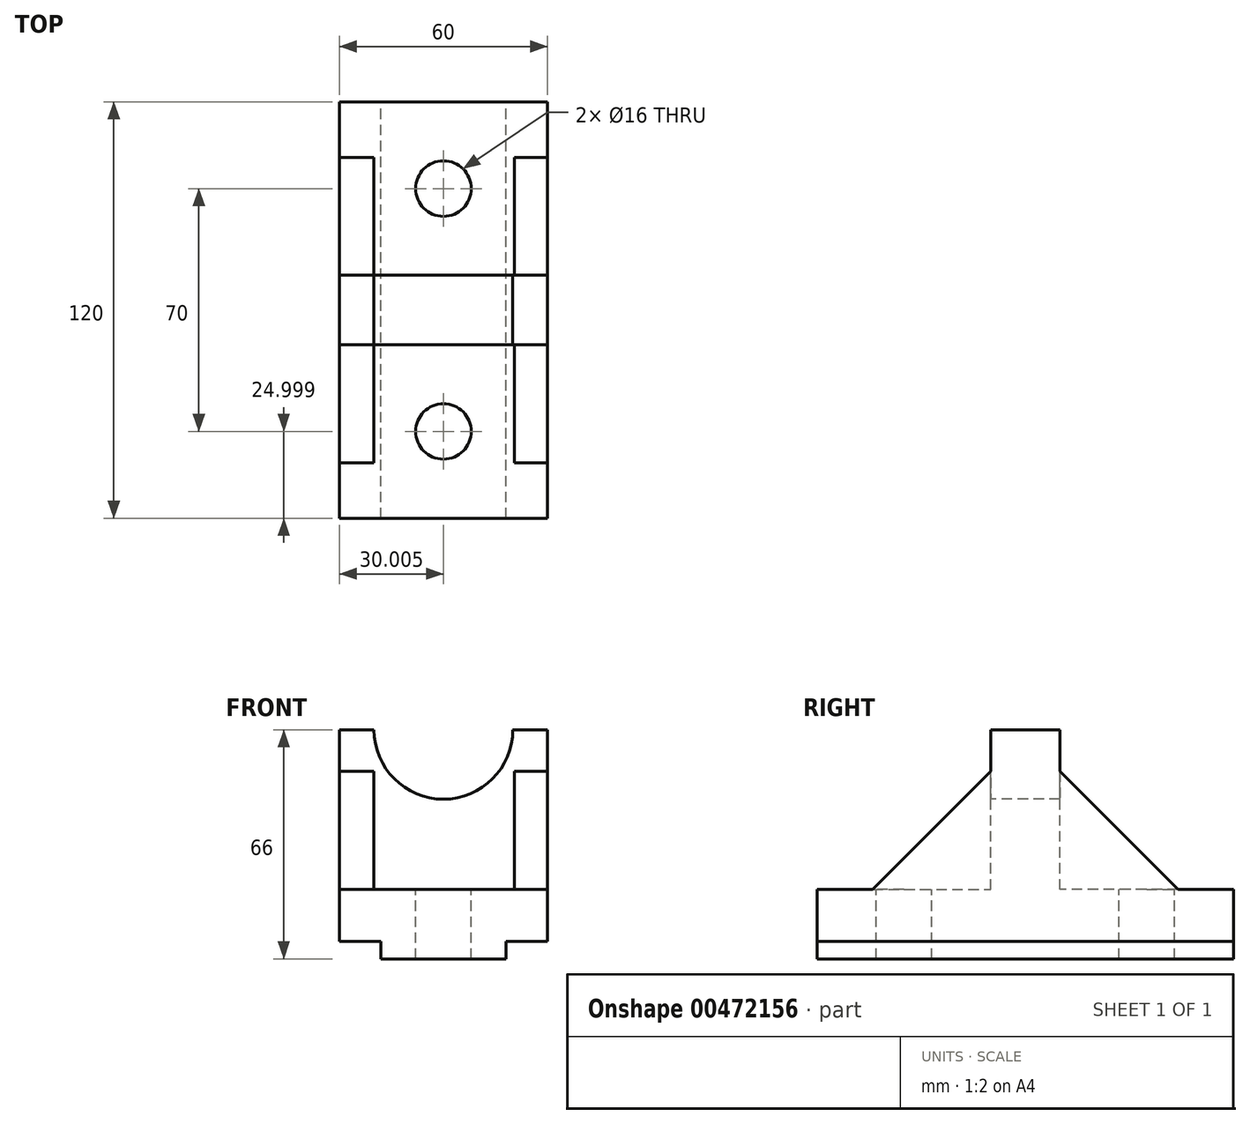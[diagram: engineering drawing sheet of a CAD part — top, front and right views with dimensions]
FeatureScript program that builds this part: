
annotation { "Feature Type Name" : "Feature", "Feature Type Description" : "" }
export const myFeature = defineFeature(function(context is Context, id is Id, definition is map)
    precondition{}
    {
        {
            var Q0;
            Q0=qCreatedBy(makeId("Top.planeOp"),FACE);
            var sketch = newSketch(context, id + "F0", { "sketchPlane" : qUnion([Q0])});
            skLineSegment(sketch, "E0.bottom", {"start": v(-50.39, 77.64) * mm, "end": v(9.61, 77.64) * mm});
            skLineSegment(sketch, "E0.top", {"start": v(-50.39, -42.36) * mm, "end": v(9.61, -42.36) * mm});
            skLineSegment(sketch, "E0.left", {"start": v(-50.39, 77.64) * mm, "end": v(-50.39, -42.36) * mm});
            skLineSegment(sketch, "E0.right", {"start": v(9.61, 77.64) * mm, "end": v(9.61, -42.36) * mm});
            skSolve(sketch);
        }
        {
            var Q0;
            Q0 = qSketchRegion(id + "F0", true);
            extrude(context, id + "F1", {"entities" : qUnion([Q0]), "depth" : 20 * mm});
        }
        {
            var Q0;
            Q0=makeQuery(id+"F1.opExtrude","SWEPT_FACE",FACE,{"disambiguationData":[OSD([sQuery(id+"F0.wireOp",EDGE,"E0.top")])]});
            var sketch = newSketch(context, id + "F2", { "sketchPlane" : qUnion([Q0])});
            skLineSegment(sketch, "E1", {"start": v(-50.39, 0) * mm, "end": v(-38.39, 0) * mm});
            skLineSegment(sketch, "E2", {"start": v(-38.39, 0) * mm, "end": v(-2.39, 0) * mm});
            skLineSegment(sketch, "E3", {"start": v(-2.39, 0) * mm, "end": v(9.61, 0) * mm});
            skSolve(sketch);
        }
        {
            var Q0;
            Q0=makeQuery(id+"F0.imprint","IMPRINT",FACE,{"disambiguationData":[TD([[makeQuery(id+"F0.imprint","IMPRINT",EDGE,{"derivedFrom":sQuery(id+"F0.wireOp",EDGE,"E0.bottom")}),-1.0]])]});
            var sketch = newSketch(context, id + "F3", { "sketchPlane" : qUnion([Q0])});
            skPoint(sketch, "E4.0", {"position": v(-2.39, -42.36) * mm});
            skPoint(sketch, "E5.0", {"position": v(-38.39, -42.36) * mm});
            skLineSegment(sketch, "E6.0", {"start": v(-50.39, 77.64) * mm, "end": v(9.61, 77.64) * mm});
            skLineSegment(sketch, "E7", {"start": v(-38.39, -42.36) * mm, "end": v(-38.39, 77.64) * mm});
            skLineSegment(sketch, "E8", {"start": v(-2.39, -42.36) * mm, "end": v(-2.39, 77.64) * mm});
            skSolve(sketch);
        }
        {
            var Q0;
            {var subQ2=sQuery(id+"F3.wireOp",EDGE,"E7");Q0=makeQuery(id+"F3.imprint","IMPRINT",FACE,{"disambiguationData":[TD([[makeQuery(id+"F3.imprint","IMPRINT",EDGE,{"derivedFrom":subQ2}),1.0]])]});}
            var Q1;
            {var subQ2=sQuery(id+"F3.wireOp",EDGE,"E8");Q1=makeQuery(id+"F3.imprint","IMPRINT",FACE,{"disambiguationData":[TD([[makeQuery(id+"F3.imprint","IMPRINT",EDGE,{"derivedFrom":subQ2}),-1.0]])]});}
            extrude(context, id + "F4", {"entities" : qUnion([Q0, Q1]), "operationType" : NewBodyOperationType.REMOVE, "depth" : 5 * mm});
        }
        {
            var Q0;
            Q0=makeQuery(id+"F1.opExtrude","CAP_FACE",FACE,{"disambiguationData":[OSD([sQuery(id+"F0.wireOp",EDGE,"E0.bottom"),sQuery(id+"F0.wireOp",EDGE,"E0.top"),sQuery(id+"F0.wireOp",EDGE,"E0.left"),sQuery(id+"F0.wireOp",EDGE,"E0.right")])],"isStart":false});
            var sketch = newSketch(context, id + "F5", { "sketchPlane" : qUnion([Q0])});
            skLineSegment(sketch, "E9", {"start": v(-20.39, -42.36) * mm, "end": v(-20.39, -17.36) * mm});
            skLineSegment(sketch, "E10", {"start": v(-20.39, -17.36) * mm, "end": v(9.61, -17.36) * mm});
            skCircle(sketch, "E11", {"center": v(-20.39, -17.36) * mm, "radius": 8 * mm});
            skLineSegment(sketch, "E12", {"start": v(-50.39, 17.64) * mm, "end": v(9.61, 17.64) * mm});
            skLineSegment(sketch, "E13.MirrorCS", {"start": v(-20.39, 7.64) * mm, "end": v(-20.39, -17.36) * mm});
            skCircle(sketch, "E14.MirrorC", {"center": v(-20.39, 52.64) * mm, "radius": 8 * mm});
            skSolve(sketch);
        }
        {
            var Q0;
            Q0 = qSketchRegion(id + "F5", true);
            extrude(context, id + "F6", {"entities" : qUnion([Q0]), "operationType" : NewBodyOperationType.REMOVE, "oppositeDirection" : true, "depth" : 45.4 * mm});
        }
        {
            var Q0;
            Q0=makeQuery(id+"F1.opExtrude","CAP_FACE",FACE,{"disambiguationData":[OSD([sQuery(id+"F0.wireOp",EDGE,"E0.bottom"),sQuery(id+"F0.wireOp",EDGE,"E0.top"),sQuery(id+"F0.wireOp",EDGE,"E0.left"),sQuery(id+"F0.wireOp",EDGE,"E0.right")])],"isStart":false});
            var sketch = newSketch(context, id + "F7", { "sketchPlane" : qUnion([Q0])});
            skLineSegment(sketch, "E15", {"start": v(-50.39, -42.36) * mm, "end": v(-50.39, 7.64) * mm});
            skLineSegment(sketch, "E16", {"start": v(-50.39, 7.64) * mm, "end": v(-50.39, 27.64) * mm});
            skLineSegment(sketch, "E17", {"start": v(-50.39, 27.64) * mm, "end": v(-50.39, 77.64) * mm});
            skLineSegment(sketch, "E18", {"start": v(-50.39, 27.64) * mm, "end": v(9.61, 27.64) * mm});
            skLineSegment(sketch, "E19", {"start": v(9.61, 27.64) * mm, "end": v(9.61, 7.64) * mm});
            skLineSegment(sketch, "E20", {"start": v(9.61, 7.64) * mm, "end": v(-50.39, 7.64) * mm});
            skSolve(sketch);
        }
        {
            var Q0;
            Q0 = qSketchRegion(id + "F7", true);
            extrude(context, id + "F8", {"entities" : qUnion([Q0]), "operationType" : NewBodyOperationType.ADD, "depth" : 46 * mm});
        }
        {
            var Q0;
            Q0=makeQuery(id+"F8.opExtrude","SWEPT_FACE",FACE,{"disambiguationData":[OSD([sQuery(id+"F7.wireOp",EDGE,"E20")])]});
            var sketch = newSketch(context, id + "F9", { "sketchPlane" : qUnion([Q0])});
            skLineSegment(sketch, "E21", {"start": v(-20.39, 66) * mm, "end": v(-20.39, 92.8) * mm});
            skLineSegment(sketch, "E22", {"start": v(-20.39, 92.8) * mm, "end": v(-20.39, 22.88) * mm});
            skSolve(sketch);
        }
        {
            var Q0;
            Q0=makeQuery(id+"F8.boolean.opBoolean","MERGE",FACE,{"derivedFrom":[makeQuery(id+"F1.opExtrude","SWEPT_FACE",FACE,{"disambiguationData":[OSD([sQuery(id+"F0.wireOp",EDGE,"E0.left")])]}),makeQuery(id+"F8.opExtrude","SWEPT_FACE",FACE,{"disambiguationData":[OSD([sQuery(id+"F7.wireOp",EDGE,"E16")])]})]});
            var sketch = newSketch(context, id + "F10", { "sketchPlane" : qUnion([Q0])});
            skLineSegment(sketch, "E23", {"start": v(42.36, 20) * mm, "end": v(-7.64, 20) * mm});
            skLineSegment(sketch, "E24", {"start": v(-48.43, -15.05) * mm, "end": v(-42.69, -15.05) * mm});
            skLineSegment(sketch, "E25", {"start": v(-7.64, 20) * mm, "end": v(-7.64, 54) * mm});
            skLineSegment(sketch, "E26", {"start": v(-7.64, 54) * mm, "end": v(26.36, 20) * mm});
            skLineSegment(sketch, "E27", {"start": v(-27.64, 54) * mm, "end": v(-61.64, 20) * mm});
            skSolve(sketch);
        }
        {
            var Q0;
            {var subQ0=sQuery(id+"F10.wireOp",EDGE,"E25");Q0=makeQuery(id+"F10.imprint","IMPRINT",FACE,{"disambiguationData":[TD([[makeQuery(id+"F10.imprint","IMPRINT",EDGE,{"derivedFrom":subQ0}),1.0]])]});}
            var Q1;
            {var subQ0=sQuery(id+"F10.wireOp",EDGE,"E27");Q1=makeQuery(id+"F10.imprint","IMPRINT",FACE,{"disambiguationData":[TD([[makeQuery(id+"F10.imprint","IMPRINT",EDGE,{"derivedFrom":subQ0}),1.0]])]});}
            extrude(context, id + "F11", {"entities" : qUnion([Q0, Q1]), "operationType" : NewBodyOperationType.ADD, "oppositeDirection" : true, "depth" : 60 * mm});
        }
        {
            var Q0;
            {var subQ0=sQuery(id+"F7.wireOp",EDGE,"E20");Q0=makeQuery(id+"F9.imprint","IMPRINT",FACE,{"disambiguationData":[TD([[makeQuery(id+"F9.imprint","IMPRINT",EDGE,{"derivedFrom":makeQuery(id+"F8.opExtrude","CAP_EDGE",EDGE,{"disambiguationData":[OSD([subQ0])],"isStart":false})}),1.0]])]});}
            var sketch = newSketch(context, id + "F12", { "sketchPlane" : qUnion([Q0])});
            skLineSegment(sketch, "E28.0", {"start": v(9.61, 66) * mm, "end": v(-50.39, 66) * mm});
            skCircle(sketch, "E29", {"center": v(-20.39, 66) * mm, "radius": 20 * mm});
            skSolve(sketch);
        }
        {
            var Q0;
            Q0 = qSketchRegion(id + "F12", true);
            extrude(context, id + "F13", {"entities" : qUnion([Q0]), "operationType" : NewBodyOperationType.REMOVE, "oppositeDirection" : true, "depth" : 212.7 * mm, "hasSecondDirection" : true, "secondDirectionOppositeDirection" : false, "secondDirectionDepth" : 25 * mm});
        }
        {
            var Q0;
            {var subQ0=sQuery(id+"F7.wireOp",EDGE,"E20");var subQ1=sQuery(id+"F7.wireOp",EDGE,"E19");var subQ2=sQuery(id+"F7.wireOp",EDGE,"E18");var subQ3=sQuery(id+"F7.wireOp",EDGE,"E16");Q0=makeQuery(id+"F13.boolean.opBoolean","SPLIT",FACE,{"disambiguationData":[TD([makeQuery(id+"F1.opExtrude","SWEPT_FACE",FACE,{"disambiguationData":[OSD([sQuery(id+"F0.wireOp",EDGE,"E0.right")])]})])],"derivedFrom":makeQuery(id+"F8.opExtrude","CAP_FACE",FACE,{"disambiguationData":[OSD([subQ3,subQ2,subQ1,subQ0])],"isStart":false})});}
            var sketch = newSketch(context, id + "F14", { "sketchPlane" : qUnion([Q0])});
            skLineSegment(sketch, "E30.0", {"start": v(-50.39, 77.64) * mm, "end": v(-50.39, -42.36) * mm});
            skLineSegment(sketch, "E31.0", {"start": v(-40.39, 27.64) * mm, "end": v(-40.39, 7.64) * mm});
            skLineSegment(sketch, "E32.0", {"start": v(-0.39, 7.64) * mm, "end": v(-0.39, 27.64) * mm});
            skLineSegment(sketch, "E33.bottom", {"start": v(-40.39, 27.64) * mm, "end": v(0, 27.64) * mm});
            skLineSegment(sketch, "E33.top", {"start": v(-40.39, 61.7) * mm, "end": v(0, 61.7) * mm});
            skLineSegment(sketch, "E33.left", {"start": v(-40.39, 27.64) * mm, "end": v(-40.39, 61.7) * mm});
            skLineSegment(sketch, "E33.right", {"start": v(0, 27.64) * mm, "end": v(0, 61.7) * mm});
            skLineSegment(sketch, "E34.bottom", {"start": v(-40.39, 7.64) * mm, "end": v(0, 7.64) * mm});
            skLineSegment(sketch, "E34.top", {"start": v(-40.39, -26.4) * mm, "end": v(0, -26.4) * mm});
            skLineSegment(sketch, "E34.left", {"start": v(-40.39, 7.64) * mm, "end": v(-40.39, -26.4) * mm});
            skLineSegment(sketch, "E34.right", {"start": v(0, 7.64) * mm, "end": v(0, -26.4) * mm});
            skSolve(sketch);
        }
        {
            var Q0;
            Q0=makeQuery(id+"F14.imprint","IMPRINT",FACE,{"disambiguationData":[TD([[makeQuery(id+"F14.imprint","IMPRINT",EDGE,{"derivedFrom":sQuery(id+"F14.wireOp",EDGE,"E33.top")}),-1.0]])]});
            var Q1;
            Q1=makeQuery(id+"F14.imprint","IMPRINT",FACE,{"disambiguationData":[TD([[makeQuery(id+"F14.imprint","IMPRINT",EDGE,{"derivedFrom":sQuery(id+"F14.wireOp",EDGE,"E34.top")}),1.0]])]});
            var Q2;
            {var subQ0=sQuery(id+"F0.wireOp",EDGE,"E0.left");var subQ1=sQuery(id+"F0.wireOp",EDGE,"E0.right");var subQ2=sQuery(id+"F0.wireOp",EDGE,"E0.bottom");Q2=makeQuery(id+"F8.boolean.opBoolean","SPLIT",FACE,{"disambiguationData":[TD([makeQuery(id+"F1.opExtrude","SWEPT_FACE",FACE,{"disambiguationData":[OSD([subQ2])]})])],"derivedFrom":makeQuery(id+"F1.opExtrude","CAP_FACE",FACE,{"disambiguationData":[OSD([subQ2,sQuery(id+"F0.wireOp",EDGE,"E0.top"),subQ0,subQ1])],"isStart":false})});}
            extrude(context, id + "F15", {"entities" : qUnion([Q0, Q1]), "operationType" : NewBodyOperationType.REMOVE, "endBound" : BoundingType.UP_TO_SURFACE, "oppositeDirection" : true, "endBoundEntityFace" : qUnion([Q2]), "depth" : 44.9 * mm});
        }
    });
